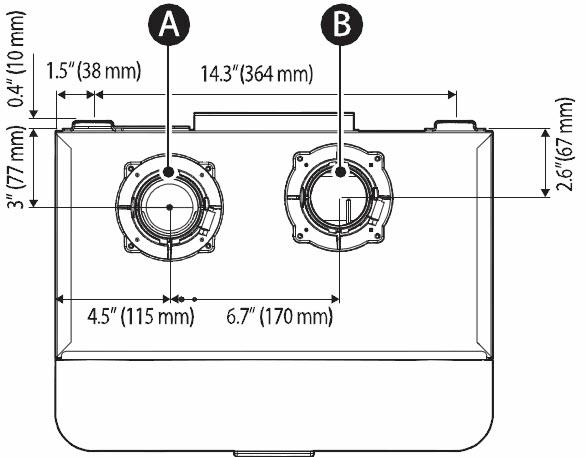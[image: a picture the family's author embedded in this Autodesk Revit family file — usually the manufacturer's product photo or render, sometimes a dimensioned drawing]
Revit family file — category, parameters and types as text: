
# Revit family: Water_Heater-Racks-Navien-NPE-4_Unit_Back_to_Back---
name_source: partatom
category: Mechanical Equipment
revit_build: Autodesk Revit 2016 (Build: 20150220_1215(x64)
units: mm (PartAtom-declared; Revit-internal decimal feet)

## family parameters
Cut with Voids When Loaded = No
Host = Face
OmniClass Number = 23.65.35.11
OmniClass Title = Supply Water Heaters
Part Type = Normal
Room Calculation Point = No
Round Connector Dimension = Use Diameter
Shared = No

## types (4) — shared parameters
2" Exhaust/Intake = Yes
3" Exhaust/Intake = No
Apparent Load = 0 VA
Assembly Code = D3010500
Certifications = Energy Star | AHRI | CSA | CSA | NFS
Cold Water Inlet = 1"
Configuration = NPE_B4_4B
Default Elevation = 48 "
Depth = 23.8 "
Description = 4 Unit Back to Back
Exhaust = 2"
Finish = Metal - Navien - White
Flow Rate = 1 GPM
Flow Rate Note = 35°F (19°C) temp rise: 11.2 GPM (42 L/m) | 45°F (25°C) temp rise: 8.7 GPM (33 L/m) | 67°F (36°C) temp rise: NPE-240A: 5.6 GPM(21 L/m), NPE-240S: 5.7 GPM(22 L/m)
Frequency = 60 Hz
Gas Inlet = 1"
Heating Capacity = 120000.0 Btu/h
Heating Capacity Note = 19,900–199,900 (BTU/H)
Height = 65.5 "
Hot Water Outlet = 1"
Ignition = Electronic ignition
Installation Type = Indoor
Intake = 2"
Keynote = 22 33 00.A1
Manifold(s) = (1) 30019042A
Manufacturer = Navien, Inc.
Manufacturer Fax Number = (949) 420-0430
Natural Gas Manifold Pressure = -0.05" WC to -0.58" WC
Natural Gas Supply Pressure = 3.5"–10.5" WC
Number of Poles = 1
Phase = 1
Power Factor = 1
Product Documentation Link = https://www.navieninc.com
Product Name = NPE Series Tankless Water Heaters w/ Racks
Product Page URL = https://www.navieninc.com
Propane Gas Manifold Pressure = -0.10" WC to -0.78" WC
Propane Gas Supply Pressure = 8"–13" WC
Rack(s) = (1) GFFM-KDIZUS-003 + (1) GFFM-KDIZUS-004
Required Cascade Operation Accessory = (4) 30014367A (Common Vent Damper & Cascade Communication Cable) or (3) GXXX000546 (Individual Vent Cascade Communication Cable)
URL = https://www.navieninc.com
Venting = Exhaust: 2" PVC, CPVC, PP, SS / 2" special gas vent type BH (Class II, A/B/C) | Intake: 2" PVC, CPVC, PP, SS / 2" special gas vent type BH (Class II, A/B/C) | Vent clearances: 0" to combustibles
Venting Type = Forced draft direct vent
Version = 2016 - v1.0.a
Voltage = 120 V
Water Pressure = 15–150 PSI
Wi-Fi Ready = NaviLink Wi-Fi Control: PBCM-AS-001
Width = 42.3 "

## per-type parameters (varying)
| type | Constraints | Model | Natural Gas | Propane Gas | Recirculation Inlet | Recirculation Inlet Visibility | Tankless Water Heaters | Weight |
| Natural Gas - Recirculating System - NPE-240A(Advanced)-NG | 6 | (4) NPE-240A-NG | Yes | No | 0" | Yes | (4) NPE-240A-NG | 82.00 lbf |
| Natural Gas - NPE-240S(Standard)-NG | 7 | (4) NPE-240S-NG | Yes | No | 1" | No | (4) NPE-240S-NG | 75.00 lbf |
| Propane Gas - Recirculating System - NPE-240A(Advanced)-LPG | 6 | (4) NPE-240A-LPG | No | Yes | 0" | Yes | (4) NPE-240A-LPG | 82.00 lbf |
| Propane Gas - NPE-240S(Standard)-LPG | 7 | (4) NPE-240S-LPG | No | Yes | 1" | No | (4) NPE-240S-LPG | 75.00 lbf |

## geometry (parser evidence)
native form markers: Sweep x15
no freeform markers — native parametric forms only
